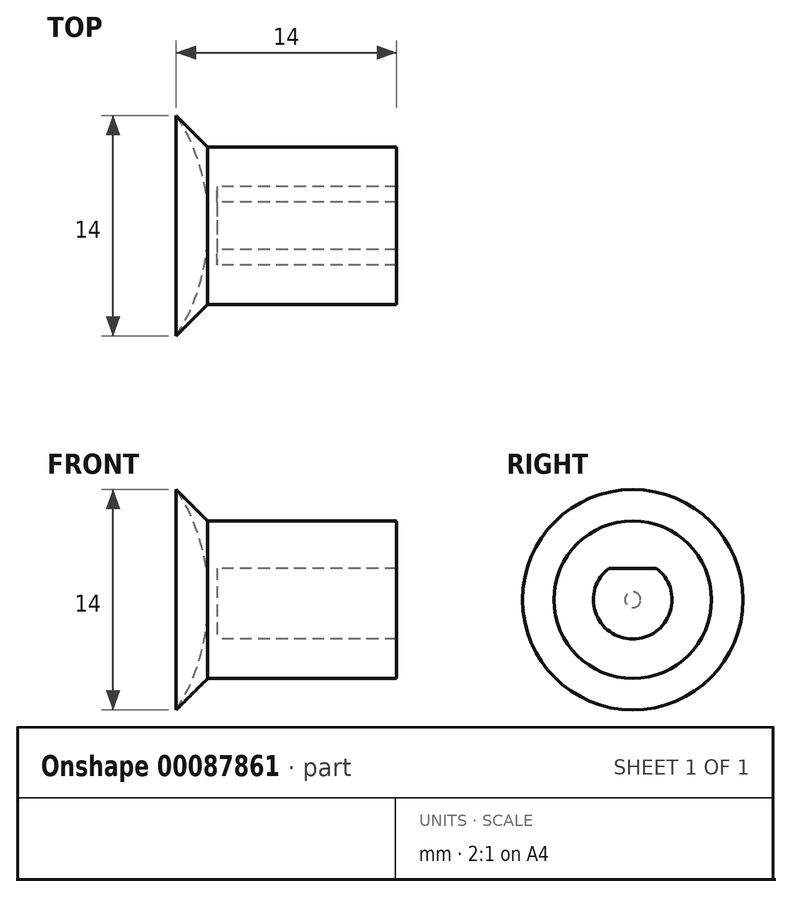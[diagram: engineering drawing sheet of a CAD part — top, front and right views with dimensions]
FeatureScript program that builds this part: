
annotation { "Feature Type Name" : "Feature", "Feature Type Description" : "" }
export const myFeature = defineFeature(function(context is Context, id is Id, definition is map)
    precondition{}
    {
        {
            var Q0;
            Q0=qCreatedBy(makeId("Right.planeOp"),FACE);
            var sketch = newSketch(context, id + "F0", { "sketchPlane" : qUnion([Q0])});
            skArc(sketch, "E0", {"start": v(-1.5, 2) * mm, "mid": v(0, -2.5) * mm, "end": v(1.5, 2) * mm});
            skCircle(sketch, "E1", {"center": v(0, 0) * mm, "radius": 5 * mm});
            skLineSegment(sketch, "E2", {"start": v(-1.5, 2) * mm, "end": v(1.5, 2) * mm});
            skSolve(sketch);
        }
        {
            var Q0;
            Q0=makeQuery(id+"F0.imprint","IMPRINT",FACE,{"disambiguationData":[TD([[makeQuery(id+"F0.imprint","IMPRINT",EDGE,{"derivedFrom":sQuery(id+"F0.wireOp",EDGE,"E0")}),-1.0]])]});
            extrude(context, id + "F1", {"entities" : qUnion([Q0]), "depth" : 12 * mm});
        }
        {
            var Q0;
            Q0=qCreatedBy(makeId("Top.planeOp"),FACE);
            var sketch = newSketch(context, id + "F2", { "sketchPlane" : qUnion([Q0])});
            skLineSegment(sketch, "E3", {"start": v(0, 5) * mm, "end": v(-2, 7) * mm});
            skArc(sketch, "E4", {"start": v(-2, 7) * mm, "mid": v(-0.47, 3.65) * mm, "end": v(0, 0) * mm});
            skLineSegment(sketch, "E5.0", {"start": v(0, 5) * mm, "end": v(0, -5) * mm});
            skLineSegment(sketch, "E6", {"start": v(0, 0) * mm, "end": v(-7.04, 0) * mm});
            skSolve(sketch);
        }
        {
            var Q0;
            Q0=makeQuery(id+"F1.opExtrude","CAP_FACE",FACE,{"disambiguationData":[OSD([sQuery(id+"F0.wireOp",EDGE,"E0"),sQuery(id+"F0.wireOp",EDGE,"E1"),sQuery(id+"F0.wireOp",EDGE,"E2")])],"isStart":true});
            var sketch = newSketch(context, id + "F3", { "sketchPlane" : qUnion([Q0])});
            skCircle(sketch, "E7.0", {"center": v(0, 0) * mm, "radius": 5 * mm});
            skSolve(sketch);
        }
        {
            var Q0;
            Q0 = qSketchRegion(id + "F3", true);
            extrude(context, id + "F4", {"entities" : qUnion([Q0]), "operationType" : NewBodyOperationType.ADD, "oppositeDirection" : true, "depth" : .6 * mm});
        }
        {
            var Q0;
            {var subQ0=sQuery(id+"F2.wireOp",EDGE,"E3");Q0=makeQuery(id+"F2.imprint","IMPRINT",FACE,{"disambiguationData":[TD([[makeQuery(id+"F2.imprint","IMPRINT",EDGE,{"derivedFrom":subQ0}),1.0]])]});}
            var Q1;
            Q1=sQuery(id+"F2.wireOp",EDGE,"E6");
            revolve(context, id + "F5", {"operationType" : NewBodyOperationType.ADD, "entities" : qUnion([Q0]), "axis" : qUnion([Q1]), "revolveType" : RevolveType.FULL});
        }
    });
